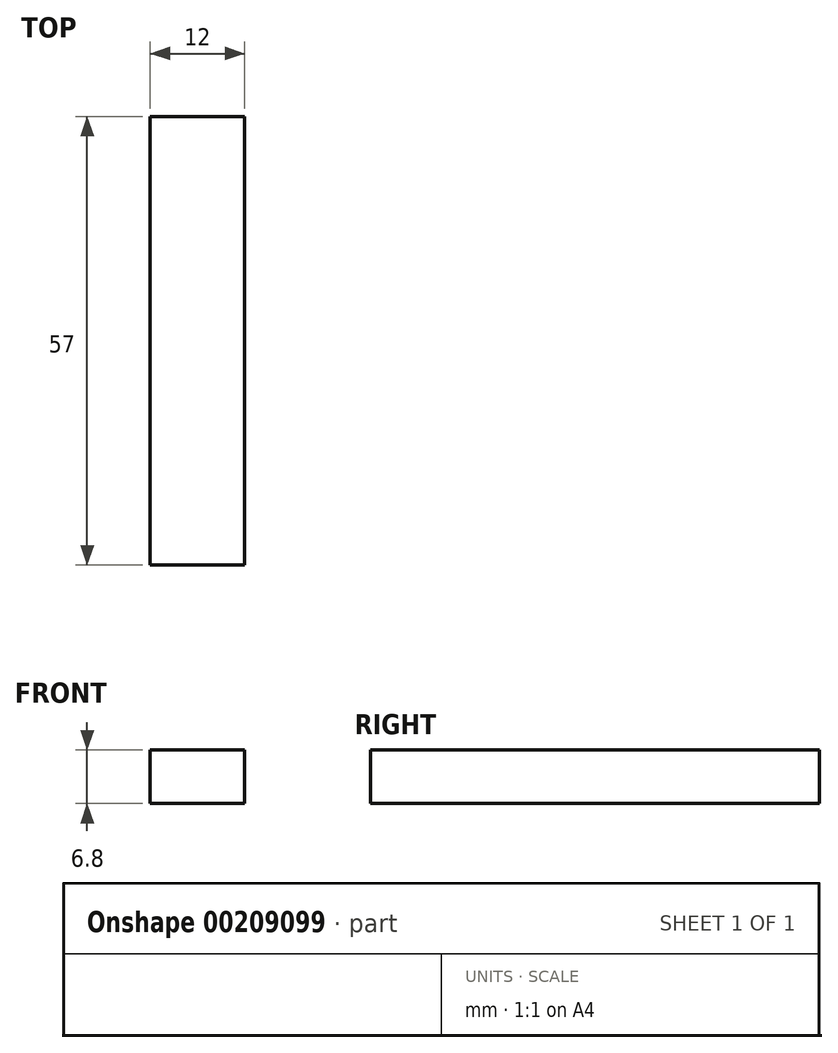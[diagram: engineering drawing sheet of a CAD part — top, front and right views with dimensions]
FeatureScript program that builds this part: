
annotation { "Feature Type Name" : "Feature", "Feature Type Description" : "" }
export const myFeature = defineFeature(function(context is Context, id is Id, definition is map)
    precondition{}
    {
        {
            var Q0;
            Q0=qCreatedBy(makeId("Top.planeOp"),FACE);
            var sketch = newSketch(context, id + "F0", { "sketchPlane" : qUnion([Q0])});
            skLineSegment(sketch, "E0.MirrorCS", {"start": v(-12.46, 33.22) * mm, "end": v(-0.46, 33.22) * mm});
            skLineSegment(sketch, "E1.MirrorCS", {"start": v(-12.46, -23.78) * mm, "end": v(-12.46, 33.22) * mm});
            skLineSegment(sketch, "E2.MirrorCS", {"start": v(-0.46, -23.78) * mm, "end": v(-0.46, 33.22) * mm});
            skLineSegment(sketch, "E3.MirrorCS", {"start": v(-12.46, -23.78) * mm, "end": v(-0.46, -23.78) * mm});
            skSolve(sketch);
        }
        {
            var Q0;
            Q0=makeQuery(id+"F0.imprint","IMPRINT",FACE,{"disambiguationData":[TD([[makeQuery(id+"F0.imprint","IMPRINT",EDGE,{"derivedFrom":sQuery(id+"F0.wireOp",EDGE,"E0.MirrorCS")}),-1.0]])]});
            extrude(context, id + "F1", {"entities" : qUnion([Q0]), "depth" : 6.8 * mm, "symmetric" : true});
        }
    });
